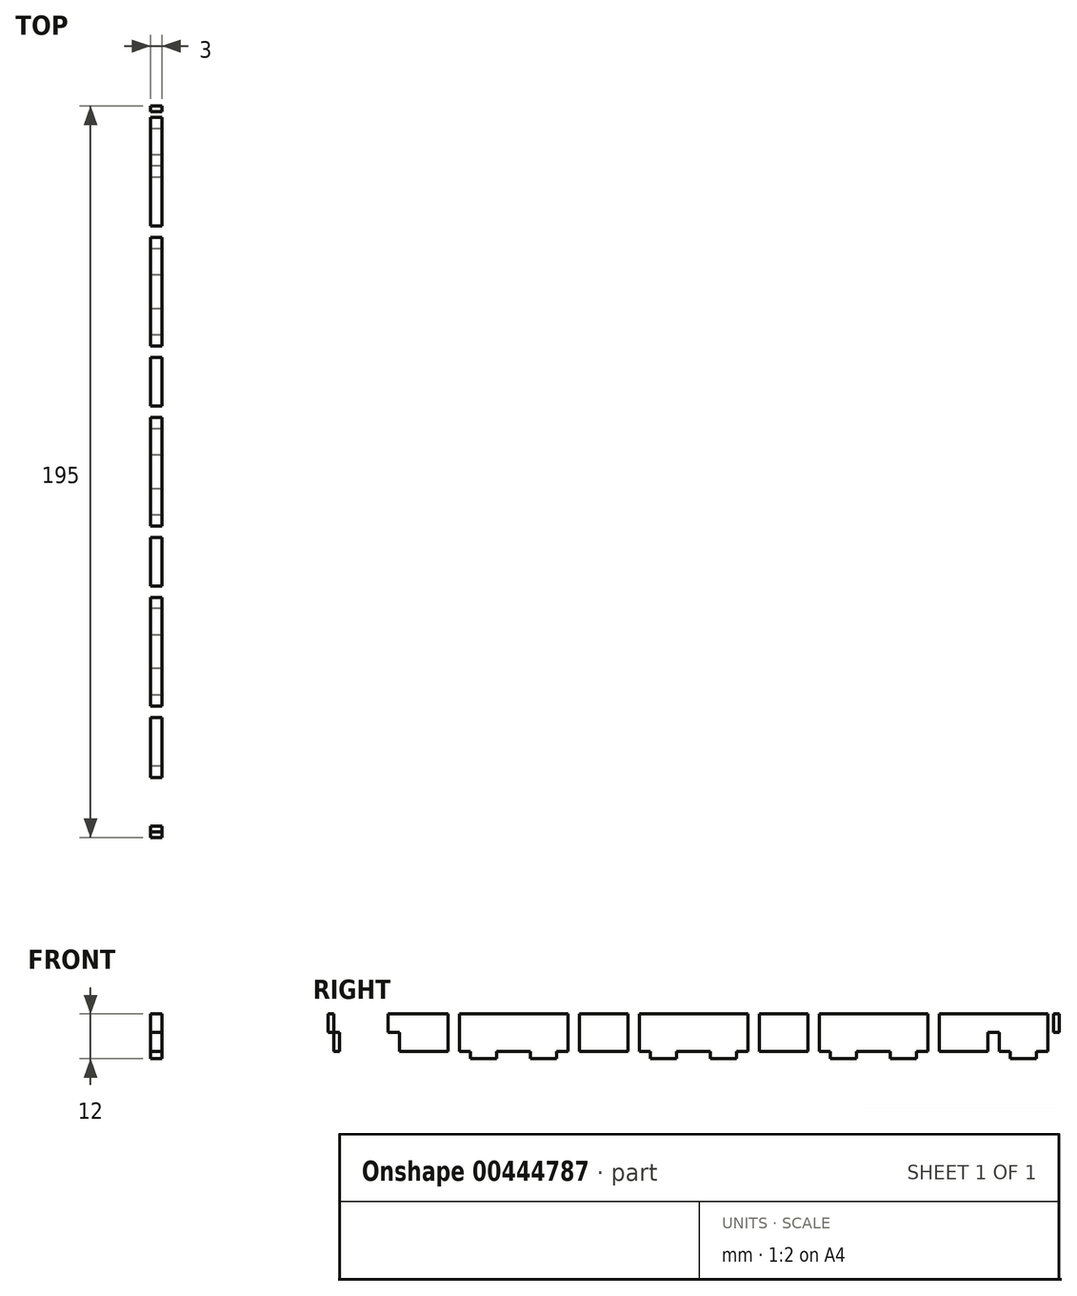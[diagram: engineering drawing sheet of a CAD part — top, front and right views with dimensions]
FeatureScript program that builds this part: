
annotation { "Feature Type Name" : "Feature", "Feature Type Description" : "" }
export const myFeature = defineFeature(function(context is Context, id is Id, definition is map)
    precondition{}
    {
        {
            var Q0;
            Q0=qCreatedBy(makeId("Right.planeOp"),FACE);
            var sketch = newSketch(context, id + "F0", { "sketchPlane" : qUnion([Q0])});
            skLineSegment(sketch, "E0", {"start": v(0, 0) * mm, "end": v(4.5, 0) * mm});
            skLineSegment(sketch, "E1", {"start": v(4.5, 0) * mm, "end": v(4.5, -2) * mm});
            skLineSegment(sketch, "E2", {"start": v(4.5, -2) * mm, "end": v(11.5, -2) * mm});
            skLineSegment(sketch, "E3", {"start": v(11.5, -2) * mm, "end": v(11.5, 0) * mm});
            skLineSegment(sketch, "E4", {"start": v(11.5, 0) * mm, "end": v(36.5, 0) * mm});
            skLineSegment(sketch, "E5", {"start": v(36.5, 0) * mm, "end": v(36.5, -2) * mm});
            skLineSegment(sketch, "E6", {"start": v(36.5, -2) * mm, "end": v(43.5, -2) * mm});
            skLineSegment(sketch, "E7", {"start": v(43.5, -2) * mm, "end": v(43.5, 0) * mm});
            skLineSegment(sketch, "E8", {"start": v(43.5, 0) * mm, "end": v(48, 0) * mm});
            skLineSegment(sketch, "E9.1.0.0", {"start": v(52.5, -2) * mm, "end": v(59.5, -2) * mm});
            skLineSegment(sketch, "E9.1.0.1", {"start": v(59.5, 0) * mm, "end": v(84.5, 0) * mm});
            skLineSegment(sketch, "E9.1.0.2", {"start": v(84.5, -2) * mm, "end": v(91.5, -2) * mm});
            skLineSegment(sketch, "E9.1.0.3", {"start": v(91.5, 0) * mm, "end": v(96, 0) * mm});
            skLineSegment(sketch, "E9.1.0.4", {"start": v(48, 0) * mm, "end": v(52.5, 0) * mm});
            skLineSegment(sketch, "E9.1.0.5", {"start": v(52.5, 0) * mm, "end": v(52.5, -2) * mm});
            skLineSegment(sketch, "E9.1.0.6", {"start": v(91.5, -2) * mm, "end": v(91.5, 0) * mm});
            skLineSegment(sketch, "E9.1.0.7", {"start": v(59.5, -2) * mm, "end": v(59.5, 0) * mm});
            skLineSegment(sketch, "E9.1.0.8", {"start": v(84.5, 0) * mm, "end": v(84.5, -2) * mm});
            skLineSegment(sketch, "E9.2.0.0", {"start": v(100.5, -2) * mm, "end": v(107.5, -2) * mm});
            skLineSegment(sketch, "E9.2.0.1", {"start": v(107.5, 0) * mm, "end": v(132.5, 0) * mm});
            skLineSegment(sketch, "E9.2.0.2", {"start": v(132.5, -2) * mm, "end": v(139.5, -2) * mm});
            skLineSegment(sketch, "E9.2.0.3", {"start": v(139.5, 0) * mm, "end": v(144, 0) * mm});
            skLineSegment(sketch, "E9.2.0.4", {"start": v(96, 0) * mm, "end": v(100.5, 0) * mm});
            skLineSegment(sketch, "E9.2.0.5", {"start": v(100.5, 0) * mm, "end": v(100.5, -2) * mm});
            skLineSegment(sketch, "E9.2.0.6", {"start": v(139.5, -2) * mm, "end": v(139.5, 0) * mm});
            skLineSegment(sketch, "E9.2.0.7", {"start": v(107.5, -2) * mm, "end": v(107.5, 0) * mm});
            skLineSegment(sketch, "E9.2.0.8", {"start": v(132.5, 0) * mm, "end": v(132.5, -2) * mm});
            skLineSegment(sketch, "E9.3.0.0", {"start": v(148.5, -2) * mm, "end": v(155.5, -2) * mm});
            skLineSegment(sketch, "E9.3.0.1", {"start": v(155.5, 0) * mm, "end": v(180.5, 0) * mm});
            skLineSegment(sketch, "E9.3.0.2", {"start": v(180.5, -2) * mm, "end": v(187.5, -2) * mm});
            skLineSegment(sketch, "E9.3.0.3", {"start": v(187.5, 0) * mm, "end": v(192, 0) * mm});
            skLineSegment(sketch, "E9.3.0.4", {"start": v(144, 0) * mm, "end": v(148.5, 0) * mm});
            skLineSegment(sketch, "E9.3.0.5", {"start": v(148.5, 0) * mm, "end": v(148.5, -2) * mm});
            skLineSegment(sketch, "E9.3.0.6", {"start": v(187.5, -2) * mm, "end": v(187.5, 0) * mm});
            skLineSegment(sketch, "E9.3.0.7", {"start": v(155.5, -2) * mm, "end": v(155.5, 0) * mm});
            skLineSegment(sketch, "E9.3.0.8", {"start": v(180.5, 0) * mm, "end": v(180.5, -2) * mm});
            skLineSegment(sketch, "E9.direction1", {"start": v(0, 0) * mm, "end": v(48, 0) * mm, "construction": true});
            skLineSegment(sketch, "E10", {"start": v(0, 0) * mm, "end": v(0, 10) * mm});
            skLineSegment(sketch, "E11", {"start": v(192, 0) * mm, "end": v(192, 10) * mm});
            skLineSegment(sketch, "E12", {"start": v(192, 10) * mm, "end": v(0, 10) * mm});
            skPoint(sketch, "E13.oppositeSnap0", {"position": v(0, 5) * mm});
            skLineSegment(sketch, "E13.bottom", {"start": v(0, 10) * mm, "end": v(-1.5, 10) * mm});
            skLineSegment(sketch, "E13.top", {"start": v(0, 5) * mm, "end": v(-1.5, 5) * mm});
            skLineSegment(sketch, "E13.left", {"start": v(0, 10) * mm, "end": v(0, 5) * mm});
            skLineSegment(sketch, "E13.right", {"start": v(-1.5, 10) * mm, "end": v(-1.5, 5) * mm});
            skPoint(sketch, "E14.oppositeSnap0", {"position": v(192, 5) * mm});
            skLineSegment(sketch, "E14.bottom", {"start": v(192, 10) * mm, "end": v(193.5, 10) * mm});
            skLineSegment(sketch, "E14.top", {"start": v(192, 5) * mm, "end": v(193.5, 5) * mm});
            skLineSegment(sketch, "E14.left", {"start": v(192, 10) * mm, "end": v(192, 5) * mm});
            skLineSegment(sketch, "E14.right", {"start": v(193.5, 10) * mm, "end": v(193.5, 5) * mm});
            skLineSegment(sketch, "E15.bottom", {"start": v(14.5, 10) * mm, "end": v(17.5, 10) * mm});
            skLineSegment(sketch, "E15.top", {"start": v(14.5, 5) * mm, "end": v(17.5, 5) * mm});
            skLineSegment(sketch, "E15.left", {"start": v(14.5, 10) * mm, "end": v(14.5, 5) * mm});
            skLineSegment(sketch, "E15.right", {"start": v(17.5, 10) * mm, "end": v(17.5, 5) * mm});
            skLineSegment(sketch, "E16.bottom", {"start": v(33.5, 10) * mm, "end": v(30.5, 10) * mm});
            skLineSegment(sketch, "E16.top", {"start": v(33.5, 5) * mm, "end": v(30.5, 5) * mm});
            skLineSegment(sketch, "E16.left", {"start": v(33.5, 10) * mm, "end": v(33.5, 5) * mm});
            skLineSegment(sketch, "E16.right", {"start": v(30.5, 10) * mm, "end": v(30.5, 5) * mm});
            skLineSegment(sketch, "E17.bottom", {"start": v(62.5, 10) * mm, "end": v(65.5, 10) * mm});
            skLineSegment(sketch, "E17.top", {"start": v(62.5, 5) * mm, "end": v(65.5, 5) * mm});
            skLineSegment(sketch, "E17.left", {"start": v(62.5, 10) * mm, "end": v(62.5, 5) * mm});
            skLineSegment(sketch, "E17.right", {"start": v(65.5, 10) * mm, "end": v(65.5, 5) * mm});
            skLineSegment(sketch, "E18.bottom", {"start": v(78.5, 10) * mm, "end": v(81.5, 10) * mm});
            skLineSegment(sketch, "E18.top", {"start": v(78.5, 5) * mm, "end": v(81.5, 5) * mm});
            skLineSegment(sketch, "E18.left", {"start": v(78.5, 10) * mm, "end": v(78.5, 5) * mm});
            skLineSegment(sketch, "E18.right", {"start": v(81.5, 10) * mm, "end": v(81.5, 5) * mm});
            skLineSegment(sketch, "E19.bottom", {"start": v(110.5, 10) * mm, "end": v(113.5, 10) * mm});
            skLineSegment(sketch, "E19.top", {"start": v(110.5, 5) * mm, "end": v(113.5, 5) * mm});
            skLineSegment(sketch, "E19.left", {"start": v(110.5, 10) * mm, "end": v(110.5, 5) * mm});
            skLineSegment(sketch, "E19.right", {"start": v(113.5, 10) * mm, "end": v(113.5, 5) * mm});
            skLineSegment(sketch, "E20.bottom", {"start": v(129.5, 10) * mm, "end": v(126.5, 10) * mm});
            skLineSegment(sketch, "E20.top", {"start": v(129.5, 5) * mm, "end": v(126.5, 5) * mm});
            skLineSegment(sketch, "E20.left", {"start": v(129.5, 10) * mm, "end": v(129.5, 5) * mm});
            skLineSegment(sketch, "E20.right", {"start": v(126.5, 10) * mm, "end": v(126.5, 5) * mm});
            skLineSegment(sketch, "E21.bottom", {"start": v(158.5, 10) * mm, "end": v(161.5, 10) * mm});
            skLineSegment(sketch, "E21.top", {"start": v(158.5, 5) * mm, "end": v(161.5, 5) * mm});
            skLineSegment(sketch, "E21.left", {"start": v(158.5, 10) * mm, "end": v(158.5, 5) * mm});
            skLineSegment(sketch, "E21.right", {"start": v(161.5, 10) * mm, "end": v(161.5, 5) * mm});
            skLineSegment(sketch, "E22.bottom", {"start": v(177.5, 10) * mm, "end": v(174.5, 10) * mm});
            skLineSegment(sketch, "E22.top", {"start": v(177.5, 5) * mm, "end": v(174.5, 5) * mm});
            skLineSegment(sketch, "E22.left", {"start": v(177.5, 10) * mm, "end": v(177.5, 5) * mm});
            skLineSegment(sketch, "E22.right", {"start": v(174.5, 10) * mm, "end": v(174.5, 5) * mm});
            skLineSegment(sketch, "E23.top", {"start": v(0, 0) * mm, "end": v(-1.5, 0) * mm});
            skLineSegment(sketch, "E23.left", {"start": v(0, 5) * mm, "end": v(0, 0) * mm});
            skLineSegment(sketch, "E23.right", {"start": v(-1.5, 5) * mm, "end": v(-1.5, 0) * mm});
            skLineSegment(sketch, "E24.top", {"start": v(14.5, 0) * mm, "end": v(17.5, 0) * mm});
            skLineSegment(sketch, "E24.left", {"start": v(14.5, 5) * mm, "end": v(14.5, 0) * mm});
            skLineSegment(sketch, "E24.right", {"start": v(17.5, 5) * mm, "end": v(17.5, 0) * mm});
            skLineSegment(sketch, "E25.bottom", {"start": v(30.5, 5) * mm, "end": v(33.5, 5) * mm});
            skLineSegment(sketch, "E25.top", {"start": v(30.5, 0) * mm, "end": v(33.5, 0) * mm});
            skLineSegment(sketch, "E25.left", {"start": v(30.5, 5) * mm, "end": v(30.5, 0) * mm});
            skLineSegment(sketch, "E25.right", {"start": v(33.5, 5) * mm, "end": v(33.5, 0) * mm});
            skLineSegment(sketch, "E26.top", {"start": v(62.5, 0) * mm, "end": v(65.5, 0) * mm});
            skLineSegment(sketch, "E26.left", {"start": v(62.5, 5) * mm, "end": v(62.5, 0) * mm});
            skLineSegment(sketch, "E26.right", {"start": v(65.5, 5) * mm, "end": v(65.5, 0) * mm});
            skLineSegment(sketch, "E27.top", {"start": v(78.5, 0) * mm, "end": v(81.5, 0) * mm});
            skLineSegment(sketch, "E27.left", {"start": v(78.5, 5) * mm, "end": v(78.5, 0) * mm});
            skLineSegment(sketch, "E27.right", {"start": v(81.5, 5) * mm, "end": v(81.5, 0) * mm});
            skLineSegment(sketch, "E28.top", {"start": v(110.5, 0) * mm, "end": v(113.5, 0) * mm});
            skLineSegment(sketch, "E28.left", {"start": v(110.5, 5) * mm, "end": v(110.5, 0) * mm});
            skLineSegment(sketch, "E28.right", {"start": v(113.5, 5) * mm, "end": v(113.5, 0) * mm});
            skLineSegment(sketch, "E29.bottom", {"start": v(126.5, 5) * mm, "end": v(129.5, 5) * mm});
            skLineSegment(sketch, "E29.top", {"start": v(126.5, 0) * mm, "end": v(129.5, 0) * mm});
            skLineSegment(sketch, "E29.left", {"start": v(126.5, 5) * mm, "end": v(126.5, 0) * mm});
            skLineSegment(sketch, "E29.right", {"start": v(129.5, 5) * mm, "end": v(129.5, 0) * mm});
            skLineSegment(sketch, "E30.top", {"start": v(158.5, 0) * mm, "end": v(161.5, 0) * mm});
            skLineSegment(sketch, "E30.left", {"start": v(158.5, 5) * mm, "end": v(158.5, 0) * mm});
            skLineSegment(sketch, "E30.right", {"start": v(161.5, 5) * mm, "end": v(161.5, 0) * mm});
            skLineSegment(sketch, "E31.bottom", {"start": v(174.5, 5) * mm, "end": v(177.5, 5) * mm});
            skLineSegment(sketch, "E31.top", {"start": v(174.5, 0) * mm, "end": v(177.5, 0) * mm});
            skLineSegment(sketch, "E31.left", {"start": v(174.5, 5) * mm, "end": v(174.5, 0) * mm});
            skLineSegment(sketch, "E31.right", {"start": v(177.5, 5) * mm, "end": v(177.5, 0) * mm});
            skLineSegment(sketch, "E32.top", {"start": v(192, 0) * mm, "end": v(193.5, 0) * mm});
            skLineSegment(sketch, "E32.left", {"start": v(192, 5) * mm, "end": v(192, 0) * mm});
            skLineSegment(sketch, "E32.right", {"start": v(193.5, 5) * mm, "end": v(193.5, 0) * mm});
            skLineSegment(sketch, "E33.bottom", {"start": v(0, 10) * mm, "end": v(1.5, 10) * mm});
            skLineSegment(sketch, "E33.top", {"start": v(0, 5) * mm, "end": v(1.5, 5) * mm});
            skLineSegment(sketch, "E33.right", {"start": v(1.5, 10) * mm, "end": v(1.5, 5) * mm});
            skLineSegment(sketch, "E34.top", {"start": v(0, 0) * mm, "end": v(1.5, 0) * mm});
            skLineSegment(sketch, "E34.right", {"start": v(1.5, 5) * mm, "end": v(1.5, 0) * mm});
            skLineSegment(sketch, "E35.bottom", {"start": v(192, 10) * mm, "end": v(190.5, 10) * mm});
            skLineSegment(sketch, "E35.top", {"start": v(192, 5) * mm, "end": v(190.5, 5) * mm});
            skLineSegment(sketch, "E35.right", {"start": v(190.5, 10) * mm, "end": v(190.5, 5) * mm});
            skLineSegment(sketch, "E36.bottom", {"start": v(190.5, 5) * mm, "end": v(192, 5) * mm});
            skLineSegment(sketch, "E36.top", {"start": v(190.5, 0) * mm, "end": v(192, 0) * mm});
            skLineSegment(sketch, "E36.left", {"start": v(190.5, 5) * mm, "end": v(190.5, 0) * mm});
            skLineSegment(sketch, "E37.bottom", {"start": v(11.5, 10) * mm, "end": v(20.5, 10) * mm});
            skLineSegment(sketch, "E37.top", {"start": v(11.5, 13) * mm, "end": v(20.5, 13) * mm});
            skLineSegment(sketch, "E37.left", {"start": v(11.5, 10) * mm, "end": v(11.5, 13) * mm});
            skLineSegment(sketch, "E37.right", {"start": v(20.5, 10) * mm, "end": v(20.5, 13) * mm});
            skLineSegment(sketch, "E38.bottom", {"start": v(171.5, 10) * mm, "end": v(180.5, 10) * mm});
            skLineSegment(sketch, "E38.top", {"start": v(171.5, 13) * mm, "end": v(180.5, 13) * mm});
            skLineSegment(sketch, "E38.left", {"start": v(171.5, 10) * mm, "end": v(171.5, 13) * mm});
            skLineSegment(sketch, "E38.right", {"start": v(180.5, 10) * mm, "end": v(180.5, 13) * mm});
            skSolve(sketch);
        }
        {
            var Q0;
            Q0=makeQuery(id+"F0.imprint","IMPRINT",FACE,{"disambiguationData":[TD([[makeQuery(id+"F0.imprint","IMPRINT",EDGE,{"derivedFrom":sQuery(id+"F0.wireOp",EDGE,"E0")}),1.0]])]});
            var Q1;
            Q1=makeQuery(id+"F0.imprint","IMPRINT",FACE,{"disambiguationData":[TD([[makeQuery(id+"F0.imprint","IMPRINT",EDGE,{"derivedFrom":sQuery(id+"F0.wireOp",EDGE,"E15.bottom")}),-1.0]])]});
            var Q2;
            {var subQ1=sQuery(id+"F0.wireOp",EDGE,"E15.right");Q2=makeQuery(id+"F0.imprint","IMPRINT",FACE,{"disambiguationData":[TD([[makeQuery(id+"F0.imprint","IMPRINT",EDGE,{"derivedFrom":subQ1}),1.0]])]});}
            var Q3;
            Q3=makeQuery(id+"F0.imprint","IMPRINT",FACE,{"disambiguationData":[TD([[makeQuery(id+"F0.imprint","IMPRINT",EDGE,{"derivedFrom":sQuery(id+"F0.wireOp",EDGE,"E16.bottom")}),1.0]])]});
            var Q4;
            {var subQ4=sQuery(id+"F0.wireOp",EDGE,"E5");Q4=makeQuery(id+"F0.imprint","IMPRINT",FACE,{"disambiguationData":[TD([[makeQuery(id+"F0.imprint","IMPRINT",EDGE,{"derivedFrom":subQ4}),1.0]])]});}
            var Q5;
            Q5=makeQuery(id+"F0.imprint","IMPRINT",FACE,{"disambiguationData":[TD([[makeQuery(id+"F0.imprint","IMPRINT",EDGE,{"derivedFrom":sQuery(id+"F0.wireOp",EDGE,"E17.bottom")}),-1.0]])]});
            var Q6;
            {var subQ0=sQuery(id+"F0.wireOp",EDGE,"E17.right");Q6=makeQuery(id+"F0.imprint","IMPRINT",FACE,{"disambiguationData":[TD([[makeQuery(id+"F0.imprint","IMPRINT",EDGE,{"derivedFrom":subQ0}),1.0]])]});}
            var Q7;
            Q7=makeQuery(id+"F0.imprint","IMPRINT",FACE,{"disambiguationData":[TD([[makeQuery(id+"F0.imprint","IMPRINT",EDGE,{"derivedFrom":sQuery(id+"F0.wireOp",EDGE,"E18.bottom")}),-1.0]])]});
            var Q8;
            Q8=makeQuery(id+"F0.imprint","IMPRINT",FACE,{"disambiguationData":[TD([[makeQuery(id+"F0.imprint","IMPRINT",EDGE,{"derivedFrom":sQuery(id+"F0.wireOp",EDGE,"E9.1.0.2")}),1.0]])]});
            var Q9;
            Q9=makeQuery(id+"F0.imprint","IMPRINT",FACE,{"disambiguationData":[TD([[makeQuery(id+"F0.imprint","IMPRINT",EDGE,{"derivedFrom":sQuery(id+"F0.wireOp",EDGE,"E19.bottom")}),-1.0]])]});
            var Q10;
            {var subQ2=sQuery(id+"F0.wireOp",EDGE,"E19.right");Q10=makeQuery(id+"F0.imprint","IMPRINT",FACE,{"disambiguationData":[TD([[makeQuery(id+"F0.imprint","IMPRINT",EDGE,{"derivedFrom":subQ2}),1.0]])]});}
            var Q11;
            Q11=makeQuery(id+"F0.imprint","IMPRINT",FACE,{"disambiguationData":[TD([[makeQuery(id+"F0.imprint","IMPRINT",EDGE,{"derivedFrom":sQuery(id+"F0.wireOp",EDGE,"E20.bottom")}),1.0]])]});
            var Q12;
            Q12=makeQuery(id+"F0.imprint","IMPRINT",FACE,{"disambiguationData":[TD([[makeQuery(id+"F0.imprint","IMPRINT",EDGE,{"derivedFrom":sQuery(id+"F0.wireOp",EDGE,"E9.2.0.2")}),1.0]])]});
            var Q13;
            Q13=makeQuery(id+"F0.imprint","IMPRINT",FACE,{"disambiguationData":[TD([[makeQuery(id+"F0.imprint","IMPRINT",EDGE,{"derivedFrom":sQuery(id+"F0.wireOp",EDGE,"E21.bottom")}),-1.0]])]});
            var Q14;
            {var subQ1=sQuery(id+"F0.wireOp",EDGE,"E21.right");Q14=makeQuery(id+"F0.imprint","IMPRINT",FACE,{"disambiguationData":[TD([[makeQuery(id+"F0.imprint","IMPRINT",EDGE,{"derivedFrom":subQ1}),1.0]])]});}
            var Q15;
            Q15=makeQuery(id+"F0.imprint","IMPRINT",FACE,{"disambiguationData":[TD([[makeQuery(id+"F0.imprint","IMPRINT",EDGE,{"derivedFrom":sQuery(id+"F0.wireOp",EDGE,"E22.bottom")}),1.0]])]});
            var Q16;
            Q16=makeQuery(id+"F0.imprint","IMPRINT",FACE,{"disambiguationData":[TD([[makeQuery(id+"F0.imprint","IMPRINT",EDGE,{"derivedFrom":sQuery(id+"F0.wireOp",EDGE,"E9.3.0.2")}),1.0]])]});
            var Q17;
            Q17=makeQuery(id+"F0.imprint","IMPRINT",FACE,{"disambiguationData":[TD([[makeQuery(id+"F0.imprint","IMPRINT",EDGE,{"derivedFrom":sQuery(id+"F0.wireOp",EDGE,"E33.bottom")}),-1.0]])]});
            var Q18;
            Q18=makeQuery(id+"F0.imprint","IMPRINT",FACE,{"disambiguationData":[TD([[makeQuery(id+"F0.imprint","IMPRINT",EDGE,{"derivedFrom":sQuery(id+"F0.wireOp",EDGE,"E35.bottom")}),1.0]])]});
            var Q19;
            Q19=makeQuery(id+"F0.imprint","IMPRINT",FACE,{"disambiguationData":[TD([[makeQuery(id+"F0.imprint","IMPRINT",EDGE,{"derivedFrom":sQuery(id+"F0.wireOp",EDGE,"E14.bottom")}),-1.0]])]});
            var Q20;
            Q20=makeQuery(id+"F0.imprint","IMPRINT",FACE,{"disambiguationData":[TD([[makeQuery(id+"F0.imprint","IMPRINT",EDGE,{"derivedFrom":sQuery(id+"F0.wireOp",EDGE,"E13.bottom")}),1.0]])]});
            var Q21;
            {var subQ0=sQuery(id+"F0.wireOp",EDGE,"E22.left");Q21=makeQuery(id+"F0.imprint","IMPRINT",FACE,{"disambiguationData":[TD([[makeQuery(id+"F0.imprint","IMPRINT",EDGE,{"derivedFrom":subQ0}),-1.0]])]});}
            var Q22;
            {var subQ0=sQuery(id+"F0.wireOp",EDGE,"E15.left");Q22=makeQuery(id+"F0.imprint","IMPRINT",FACE,{"disambiguationData":[TD([[makeQuery(id+"F0.imprint","IMPRINT",EDGE,{"derivedFrom":subQ0}),1.0]])]});}
            extrude(context, id + "F1", {"entities" : qUnion([Q0, Q1, Q2, Q3, Q4, Q5, Q6, Q7, Q8, Q9, Q10, Q11, Q12, Q13, Q14, Q15, Q16, Q17, Q18, Q19, Q20, Q21, Q22]), "depth" : 3 * mm});
        }
    });
